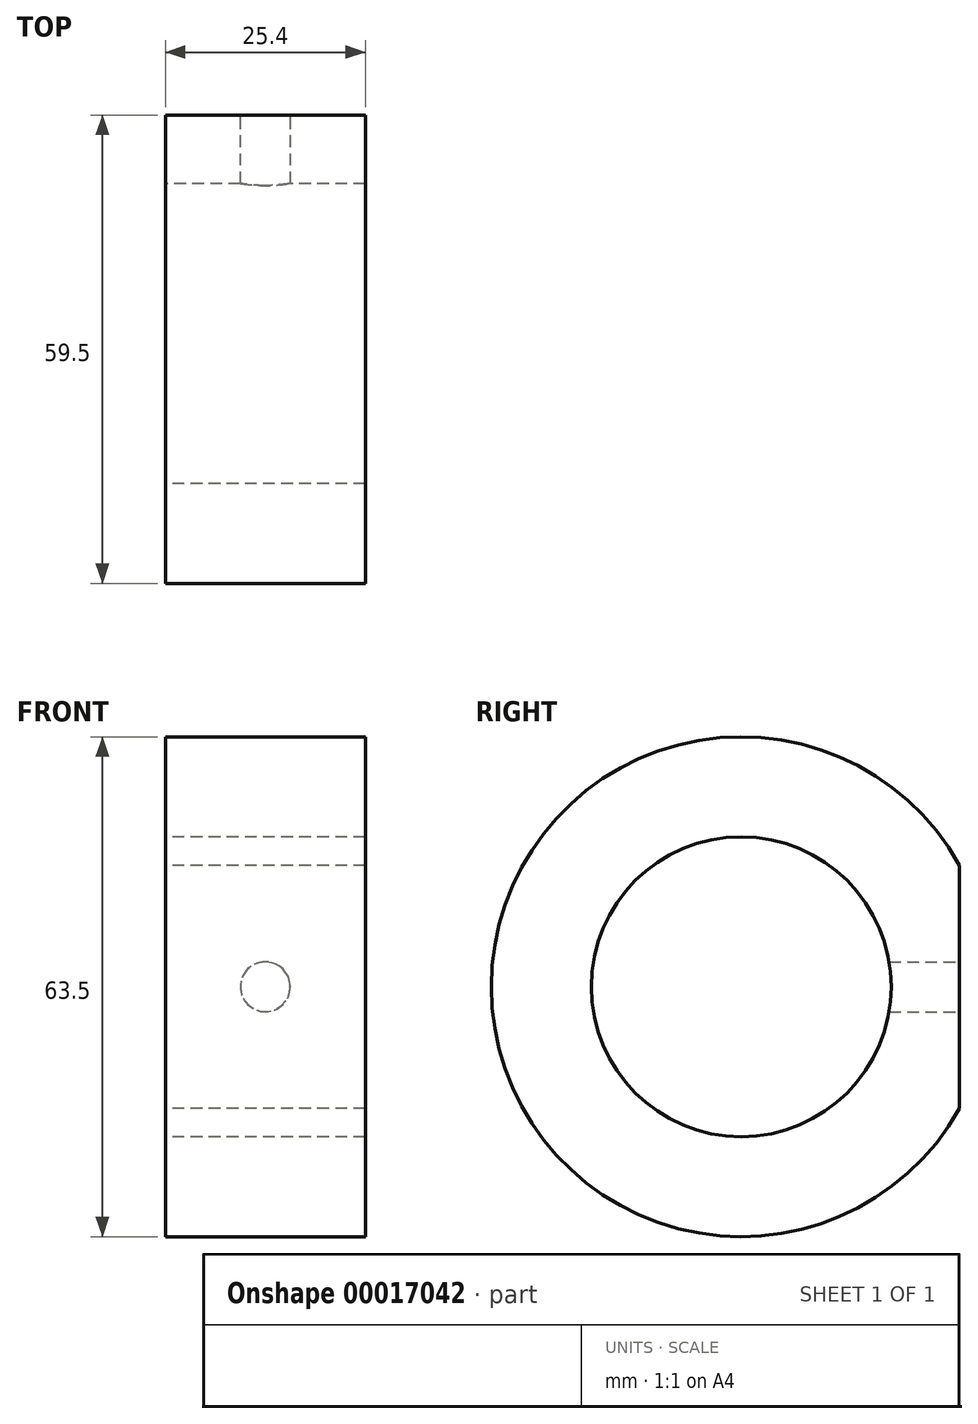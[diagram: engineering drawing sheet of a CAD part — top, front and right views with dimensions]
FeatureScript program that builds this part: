
annotation { "Feature Type Name" : "Feature", "Feature Type Description" : "" }
export const myFeature = defineFeature(function(context is Context, id is Id, definition is map)
    precondition{}
    {
        {
            var Q0;
            Q0=qCreatedBy(makeId("Right.planeOp"),FACE);
            var sketch = newSketch(context, id + "F0", { "sketchPlane" : qUnion([Q0])});
            skCircle(sketch, "E0", {"center": v(0, 0) * mm, "radius": 19.05 * mm});
            skArc(sketch, "E1", {"start": v(27.75, 15.43) * mm, "mid": v(-31.75, 0) * mm, "end": v(27.75, -15.43) * mm});
            skLineSegment(sketch, "E2", {"start": v(27.75, 15.43) * mm, "end": v(27.75, -15.43) * mm});
            skSolve(sketch);
        }
        {
            var Q0;
            Q0 = qSketchRegion(id + "F0", true);
            extrude(context, id + "F1", {"entities" : qUnion([Q0]), "depth" : 25.4 * mm});
        }
        {
            var Q0;
            Q0=makeQuery(id+"F1.opExtrude","SWEPT_FACE",FACE,{"disambiguationData":[OSD([sQuery(id+"F0.wireOp",EDGE,"E2")])]});
            var sketch = newSketch(context, id + "F2", { "sketchPlane" : qUnion([Q0])});
            skCircle(sketch, "E3", {"center": v(-12.7, 0) * mm, "radius": 3.18 * mm});
            skSolve(sketch);
        }
        {
            var Q0;
            Q0 = qSketchRegion(id + "F2", true);
            extrude(context, id + "F3", {"entities" : qUnion([Q0]), "operationType" : NewBodyOperationType.REMOVE, "oppositeDirection" : true, "depth" : 25.4 * mm});
        }
    });
